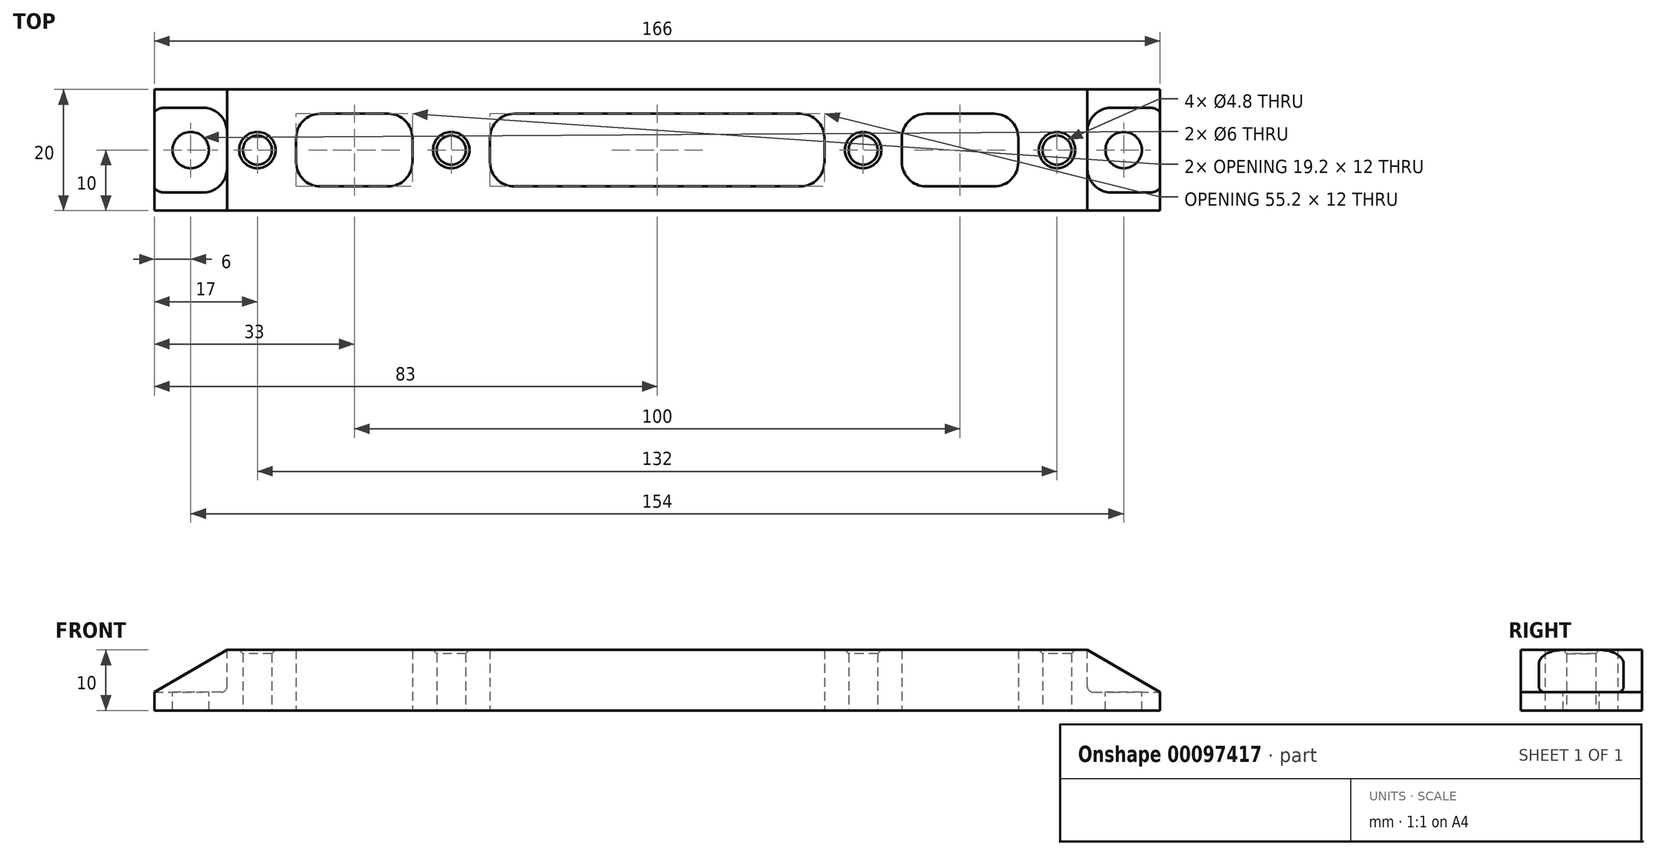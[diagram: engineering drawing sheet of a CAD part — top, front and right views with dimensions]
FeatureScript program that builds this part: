
annotation { "Feature Type Name" : "Feature", "Feature Type Description" : "" }
export const myFeature = defineFeature(function(context is Context, id is Id, definition is map)
    precondition{}
    {
        {
            var Q0;
            Q0=qCreatedBy(makeId("Top.planeOp"),FACE);
            var sketch = newSketch(context, id + "F0", { "sketchPlane" : qUnion([Q0])});
            skLineSegment(sketch, "E0.bottom", {"start": v(0, 0) * mm, "end": v(166, 0) * mm});
            skLineSegment(sketch, "E0.top", {"start": v(0, 20) * mm, "end": v(166, 20) * mm});
            skLineSegment(sketch, "E0.left", {"start": v(0, 0) * mm, "end": v(0, 20) * mm});
            skLineSegment(sketch, "E0.right", {"start": v(166, 0) * mm, "end": v(166, 20) * mm});
            skLineSegment(sketch, "E1", {"start": v(166, 10) * mm, "end": v(0, 10) * mm, "construction": true});
            skLineSegment(sketch, "E2", {"start": v(83, 0) * mm, "end": v(83, 20) * mm, "construction": true});
            skCircle(sketch, "E3", {"center": v(17, 10) * mm, "radius": 2.4 * mm});
            skCircle(sketch, "E4", {"center": v(49, 10) * mm, "radius": 2.4 * mm});
            skCircle(sketch, "E5", {"center": v(149, 10) * mm, "radius": 2.4 * mm});
            skCircle(sketch, "E6", {"center": v(117, 10) * mm, "radius": 2.4 * mm});
            skSolve(sketch);
        }
        {
            var Q0;
            Q0=makeQuery(id+"F0.imprint","IMPRINT",FACE,{"disambiguationData":[TD([[makeQuery(id+"F0.imprint","IMPRINT",EDGE,{"derivedFrom":sQuery(id+"F0.wireOp",EDGE,"E0.bottom")}),1.0]])]});
            extrude(context, id + "F1", {"entities" : qUnion([Q0]), "depth" : 10 * mm});
        }
        {
            var Q0;
            Q0=makeQuery(id+"F1.opExtrude","CAP_FACE",FACE,{"disambiguationData":[OSD([sQuery(id+"F0.wireOp",EDGE,"E0.bottom"),sQuery(id+"F0.wireOp",EDGE,"E0.top"),sQuery(id+"F0.wireOp",EDGE,"E0.left"),sQuery(id+"F0.wireOp",EDGE,"E0.right"),sQuery(id+"F0.wireOp",EDGE,"E3"),sQuery(id+"F0.wireOp",EDGE,"E4"),sQuery(id+"F0.wireOp",EDGE,"E5"),sQuery(id+"F0.wireOp",EDGE,"E6")])],"isStart":false});
            var sketch = newSketch(context, id + "F2", { "sketchPlane" : qUnion([Q0])});
            skLineSegment(sketch, "E7", {"start": v(0, 17) * mm, "end": v(12, 17) * mm});
            skLineSegment(sketch, "E8", {"start": v(12, 17) * mm, "end": v(12, 3) * mm});
            skLineSegment(sketch, "E9", {"start": v(12, 3) * mm, "end": v(0, 3) * mm});
            skLineSegment(sketch, "E10", {"start": v(0, 3) * mm, "end": v(0, 17) * mm});
            skLineSegment(sketch, "E11", {"start": v(166, 17) * mm, "end": v(154, 17) * mm});
            skLineSegment(sketch, "E12", {"start": v(154, 17) * mm, "end": v(154, 3) * mm});
            skLineSegment(sketch, "E13", {"start": v(154, 3) * mm, "end": v(166, 3) * mm});
            skLineSegment(sketch, "E14", {"start": v(166, 3) * mm, "end": v(166, 17) * mm});
            skSolve(sketch);
        }
        {
            var Q0;
            Q0 = qSketchRegion(id + "F2", true);
            extrude(context, id + "F3", {"entities" : qUnion([Q0]), "operationType" : NewBodyOperationType.REMOVE, "oppositeDirection" : true, "depth" : 7 * mm});
        }
        {
            var Q0;
            Q0=makeQuery(id+"F3.boolean.opBoolean","COPY",FACE,{"derivedFrom":makeQuery(id+"F3.opExtrude","SWEPT_FACE",FACE,{"disambiguationData":[OSD([sQuery(id+"F2.wireOp",EDGE,"E7")])]})});
            var sketch = newSketch(context, id + "F4", { "sketchPlane" : qUnion([Q0])});
            skLineSegment(sketch, "E15", {"start": v(0, 3) * mm, "end": v(12, 10) * mm});
            skLineSegment(sketch, "E16.0", {"start": v(0, 10) * mm, "end": v(12, 10) * mm});
            skLineSegment(sketch, "E16.1", {"start": v(0, 3) * mm, "end": v(0, 10) * mm});
            skLineSegment(sketch, "E17.0", {"start": v(166, 10) * mm, "end": v(154, 10) * mm});
            skLineSegment(sketch, "E17.1", {"start": v(166, 3) * mm, "end": v(166, 10) * mm});
            skLineSegment(sketch, "E18", {"start": v(154, 10) * mm, "end": v(166, 3) * mm});
            skSolve(sketch);
        }
        {
            var Q0;
            Q0 = qSketchRegion(id + "F4", true);
            extrude(context, id + "F5", {"entities" : qUnion([Q0]), "operationType" : NewBodyOperationType.REMOVE, "endBound" : BoundingType.THROUGH_ALL, "oppositeDirection" : true, "depth" : 25 * mm, "hasSecondDirection" : true, "secondDirectionBound" : SecondDirectionBoundingType.THROUGH_ALL, "secondDirectionOppositeDirection" : false, "secondDirectionDepth" : 25 * mm});
        }
        {
            var Q0;
            Q0=makeQuery(id+"F3.boolean.opBoolean","COPY",EDGE,{"derivedFrom":makeQuery(id+"F3.opExtrude","SWEPT_EDGE",EDGE,{"disambiguationData":[OSD([sQuery(id+"F2.wireOp",EDGE,"E7"),sQuery(id+"F2.wireOp",EDGE,"E8")])]})});
            var Q1;
            Q1=makeQuery(id+"F3.boolean.opBoolean","COPY",EDGE,{"derivedFrom":makeQuery(id+"F3.opExtrude","SWEPT_EDGE",EDGE,{"disambiguationData":[OSD([sQuery(id+"F2.wireOp",EDGE,"E8"),sQuery(id+"F2.wireOp",EDGE,"E9")])]})});
            var Q2;
            Q2=makeQuery(id+"F3.boolean.opBoolean","COPY",EDGE,{"derivedFrom":makeQuery(id+"F3.opExtrude","SWEPT_EDGE",EDGE,{"disambiguationData":[OSD([sQuery(id+"F2.wireOp",EDGE,"E12"),sQuery(id+"F2.wireOp",EDGE,"E13")])]})});
            var Q3;
            Q3=makeQuery(id+"F3.boolean.opBoolean","COPY",EDGE,{"derivedFrom":makeQuery(id+"F3.opExtrude","SWEPT_EDGE",EDGE,{"disambiguationData":[OSD([sQuery(id+"F2.wireOp",EDGE,"E11"),sQuery(id+"F2.wireOp",EDGE,"E12")])]})});
            fillet(context, id + "F6", {"entities" : qUnion([Q0, Q1, Q2, Q3]), "radius" : 4 * mm, "tangentPropagation" : true, "allowEdgeOverflow" : false});
        }
        {
            var Q0;
            Q0=makeQuery(id+"F3.boolean.opBoolean","COPY",EDGE,{"derivedFrom":makeQuery(id+"F3.opExtrude","CAP_EDGE",EDGE,{"disambiguationData":[OSD([sQuery(id+"F2.wireOp",EDGE,"E11")])],"isStart":false})});
            var Q1;
            Q1=makeQuery(id+"F3.boolean.opBoolean","COPY",EDGE,{"derivedFrom":makeQuery(id+"F3.opExtrude","CAP_EDGE",EDGE,{"disambiguationData":[OSD([sQuery(id+"F2.wireOp",EDGE,"E9")])],"isStart":false})});
            fillet(context, id + "F7", {"entities" : qUnion([Q0, Q1]), "radius" : 1 * mm, "tangentPropagation" : true, "allowEdgeOverflow" : false});
        }
        {
            var Q0;
            Q0=makeQuery(id+"F3.boolean.opBoolean","COPY",FACE,{"derivedFrom":makeQuery(id+"F3.opExtrude","CAP_FACE",FACE,{"disambiguationData":[OSD([sQuery(id+"F2.wireOp",EDGE,"E11"),sQuery(id+"F2.wireOp",EDGE,"E12"),sQuery(id+"F2.wireOp",EDGE,"E13"),sQuery(id+"F2.wireOp",EDGE,"E14")])],"isStart":false})});
            var sketch = newSketch(context, id + "F8", { "sketchPlane" : qUnion([Q0])});
            skLineSegment(sketch, "E19", {"start": v(166, 10) * mm, "end": v(0, 10) * mm, "construction": true});
            skCircle(sketch, "E20", {"center": v(160, 10) * mm, "radius": 3 * mm});
            skLineSegment(sketch, "E21", {"start": v(83, 10) * mm, "end": v(83, -8.6) * mm, "construction": true});
            skPoint(sketch, "E21.endSnap0", {"position": v(83, 10) * mm});
            skCircle(sketch, "E22", {"center": v(6, 10) * mm, "radius": 3 * mm});
            skSolve(sketch);
        }
        {
            var Q0;
            Q0 = qSketchRegion(id + "F8", true);
            extrude(context, id + "F9", {"entities" : qUnion([Q0]), "operationType" : NewBodyOperationType.REMOVE, "endBound" : BoundingType.THROUGH_ALL, "oppositeDirection" : true, "depth" : 25 * mm});
        }
        {
            var Q0;
            Q0=makeQuery(id+"F1.opExtrude","CAP_FACE",FACE,{"disambiguationData":[OSD([sQuery(id+"F0.wireOp",EDGE,"E0.bottom"),sQuery(id+"F0.wireOp",EDGE,"E0.top"),sQuery(id+"F0.wireOp",EDGE,"E0.left"),sQuery(id+"F0.wireOp",EDGE,"E0.right"),sQuery(id+"F0.wireOp",EDGE,"E3"),sQuery(id+"F0.wireOp",EDGE,"E4"),sQuery(id+"F0.wireOp",EDGE,"E5"),sQuery(id+"F0.wireOp",EDGE,"E6")])],"isStart":true});
            var sketch = newSketch(context, id + "F10", { "sketchPlane" : qUnion([Q0])});
            skLineSegment(sketch, "E23", {"start": v(110.6, -16) * mm, "end": v(110.6, -4) * mm});
            skLineSegment(sketch, "E24", {"start": v(110.6, -4) * mm, "end": v(55.4, -4) * mm});
            skLineSegment(sketch, "E25", {"start": v(55.4, -4) * mm, "end": v(55.4, -16) * mm});
            skLineSegment(sketch, "E26", {"start": v(55.4, -16) * mm, "end": v(110.6, -16) * mm});
            skLineSegment(sketch, "E27", {"start": v(142.6, -16) * mm, "end": v(123.4, -16) * mm});
            skLineSegment(sketch, "E28", {"start": v(123.4, -16) * mm, "end": v(123.4, -4) * mm});
            skLineSegment(sketch, "E29", {"start": v(123.4, -4) * mm, "end": v(142.6, -4) * mm});
            skLineSegment(sketch, "E30", {"start": v(142.6, -4) * mm, "end": v(142.6, -16) * mm});
            skLineSegment(sketch, "E31.bottom", {"start": v(42.6, -16) * mm, "end": v(23.4, -16) * mm});
            skLineSegment(sketch, "E31.top", {"start": v(42.6, -4) * mm, "end": v(23.4, -4) * mm});
            skLineSegment(sketch, "E31.left", {"start": v(42.6, -16) * mm, "end": v(42.6, -4) * mm});
            skLineSegment(sketch, "E31.right", {"start": v(23.4, -16) * mm, "end": v(23.4, -4) * mm});
            skSolve(sketch);
        }
        {
            var Q0;
            Q0 = qSketchRegion(id + "F10", true);
            extrude(context, id + "F11", {"entities" : qUnion([Q0]), "operationType" : NewBodyOperationType.REMOVE, "endBound" : BoundingType.THROUGH_ALL, "oppositeDirection" : true, "depth" : 6 * mm});
        }
        {
            var Q0;
            Q0=makeQuery(id+"F11.boolean.opBoolean","COPY",EDGE,{"derivedFrom":makeQuery(id+"F11.opExtrude","SWEPT_EDGE",EDGE,{"disambiguationData":[OSD([sQuery(id+"F10.wireOp",EDGE,"E27"),sQuery(id+"F10.wireOp",EDGE,"E28")])]})});
            var Q1;
            Q1=makeQuery(id+"F11.boolean.opBoolean","COPY",EDGE,{"derivedFrom":makeQuery(id+"F11.opExtrude","SWEPT_EDGE",EDGE,{"disambiguationData":[OSD([sQuery(id+"F10.wireOp",EDGE,"E28"),sQuery(id+"F10.wireOp",EDGE,"E29")])]})});
            var Q2;
            Q2=makeQuery(id+"F11.boolean.opBoolean","COPY",EDGE,{"derivedFrom":makeQuery(id+"F11.opExtrude","SWEPT_EDGE",EDGE,{"disambiguationData":[OSD([sQuery(id+"F10.wireOp",EDGE,"E27"),sQuery(id+"F10.wireOp",EDGE,"E30")])]})});
            var Q3;
            Q3=makeQuery(id+"F11.boolean.opBoolean","COPY",EDGE,{"derivedFrom":makeQuery(id+"F11.opExtrude","SWEPT_EDGE",EDGE,{"disambiguationData":[OSD([sQuery(id+"F10.wireOp",EDGE,"E29"),sQuery(id+"F10.wireOp",EDGE,"E30")])]})});
            var Q4;
            Q4=makeQuery(id+"F11.boolean.opBoolean","COPY",EDGE,{"derivedFrom":makeQuery(id+"F11.opExtrude","SWEPT_EDGE",EDGE,{"disambiguationData":[OSD([sQuery(id+"F10.wireOp",EDGE,"E23"),sQuery(id+"F10.wireOp",EDGE,"E26")])]})});
            var Q5;
            Q5=makeQuery(id+"F11.boolean.opBoolean","COPY",EDGE,{"derivedFrom":makeQuery(id+"F11.opExtrude","SWEPT_EDGE",EDGE,{"disambiguationData":[OSD([sQuery(id+"F10.wireOp",EDGE,"E23"),sQuery(id+"F10.wireOp",EDGE,"E24")])]})});
            var Q6;
            Q6=makeQuery(id+"F11.boolean.opBoolean","COPY",EDGE,{"derivedFrom":makeQuery(id+"F11.opExtrude","SWEPT_EDGE",EDGE,{"disambiguationData":[OSD([sQuery(id+"F10.wireOp",EDGE,"E25"),sQuery(id+"F10.wireOp",EDGE,"E26")])]})});
            var Q7;
            Q7=makeQuery(id+"F11.boolean.opBoolean","COPY",EDGE,{"derivedFrom":makeQuery(id+"F11.opExtrude","SWEPT_EDGE",EDGE,{"disambiguationData":[OSD([sQuery(id+"F10.wireOp",EDGE,"E24"),sQuery(id+"F10.wireOp",EDGE,"E25")])]})});
            var Q8;
            Q8=makeQuery(id+"F11.boolean.opBoolean","COPY",EDGE,{"derivedFrom":makeQuery(id+"F11.opExtrude","SWEPT_EDGE",EDGE,{"disambiguationData":[OSD([sQuery(id+"F10.wireOp",EDGE,"E31.top"),sQuery(id+"F10.wireOp",EDGE,"E31.left")])]})});
            var Q9;
            Q9=makeQuery(id+"F11.boolean.opBoolean","COPY",EDGE,{"derivedFrom":makeQuery(id+"F11.opExtrude","SWEPT_EDGE",EDGE,{"disambiguationData":[OSD([sQuery(id+"F10.wireOp",EDGE,"E31.bottom"),sQuery(id+"F10.wireOp",EDGE,"E31.left")])]})});
            var Q10;
            Q10=makeQuery(id+"F11.boolean.opBoolean","COPY",EDGE,{"derivedFrom":makeQuery(id+"F11.opExtrude","SWEPT_EDGE",EDGE,{"disambiguationData":[OSD([sQuery(id+"F10.wireOp",EDGE,"E31.bottom"),sQuery(id+"F10.wireOp",EDGE,"E31.right")])]})});
            var Q11;
            Q11=makeQuery(id+"F11.boolean.opBoolean","COPY",EDGE,{"derivedFrom":makeQuery(id+"F11.opExtrude","SWEPT_EDGE",EDGE,{"disambiguationData":[OSD([sQuery(id+"F10.wireOp",EDGE,"E31.top"),sQuery(id+"F10.wireOp",EDGE,"E31.right")])]})});
            fillet(context, id + "F12", {"entities" : qUnion([Q0, Q1, Q2, Q3, Q4, Q5, Q6, Q7, Q8, Q9, Q10, Q11]), "radius" : 4 * mm, "tangentPropagation" : true, "allowEdgeOverflow" : false});
        }
        {
            var Q0;
            Q0=makeQuery(id+"F9.boolean.opBoolean","COPY",EDGE,{"derivedFrom":makeQuery(id+"F9.opExtrude","CAP_EDGE",EDGE,{"disambiguationData":[OSD([sQuery(id+"F8.wireOp",EDGE,"E22")])],"isStart":true})});
            var Q1;
            Q1=makeQuery(id+"F1.opExtrude","CAP_EDGE",EDGE,{"disambiguationData":[OSD([sQuery(id+"F0.wireOp",EDGE,"E3")])],"isStart":false});
            var Q2;
            Q2=makeQuery(id+"F1.opExtrude","CAP_EDGE",EDGE,{"disambiguationData":[OSD([sQuery(id+"F0.wireOp",EDGE,"E4")])],"isStart":false});
            var Q3;
            Q3=makeQuery(id+"F1.opExtrude","CAP_EDGE",EDGE,{"disambiguationData":[OSD([sQuery(id+"F0.wireOp",EDGE,"E6")])],"isStart":false});
            var Q4;
            Q4=makeQuery(id+"F1.opExtrude","CAP_EDGE",EDGE,{"disambiguationData":[OSD([sQuery(id+"F0.wireOp",EDGE,"E5")])],"isStart":false});
            var Q5;
            Q5=makeQuery(id+"F9.boolean.opBoolean","COPY",EDGE,{"derivedFrom":makeQuery(id+"F9.opExtrude","CAP_EDGE",EDGE,{"disambiguationData":[OSD([sQuery(id+"F8.wireOp",EDGE,"E20")])],"isStart":true})});
            chamfer(context, id + "F13", {"entities" : qUnion([Q0, Q1, Q2, Q3, Q4, Q5]), "width" : 0.6 * mm, "tangentPropagation" : true});
        }
    });
